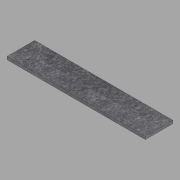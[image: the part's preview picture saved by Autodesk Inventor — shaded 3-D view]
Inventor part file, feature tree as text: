
AUTODESK INVENTOR PART (.ipt)
format: ipt  version: 2022.2 (Build 262287000, 287)  size: 99,328 bytes
history: native  units: in
note: dims shown in document units (in); Inventor stores cm internally (conversion verified against a paired STEP export)
features: extrude x1, sketch x1
ambient origin geometry x8: Origin, YZ Plane, XZ Plane, XY Plane, X Axis, Y Axis, Z Axis, Center Point
bodies: Solid1 (feature_tree)
feature tree (2):
  extrude  "Extrusion1"  Depth=12.0in
  sketch  "Sketch1"  dims[d0=60.0in d1=12.0in d2=1.25in d3=0.0in]
